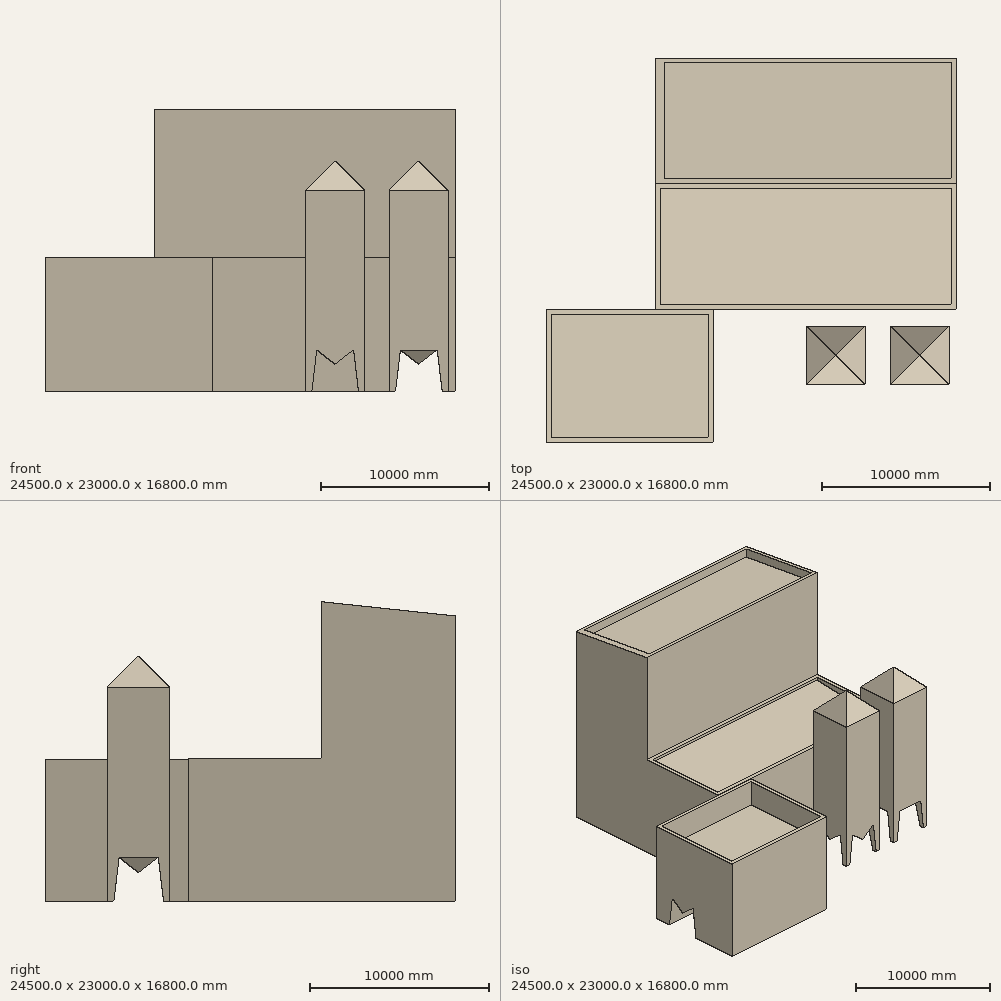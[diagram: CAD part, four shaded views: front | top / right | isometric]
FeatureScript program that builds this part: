
annotation { "Feature Type Name" : "Feature", "Feature Type Description" : "" }
export const myFeature = defineFeature(function(context is Context, id is Id, definition is map)
    precondition{}
    {
        {
            var Q0;
            Q0=qCreatedBy(makeId("Top.planeOp"),FACE);
            var sketch = newSketch(context, id + "F0", { "sketchPlane" : qUnion([Q0])});
            skLineSegment(sketch, "E0.bottom", {"start": v(0, 0) * mm, "end": v(18000, 0) * mm});
            skLineSegment(sketch, "E0.top", {"start": v(0, 7500) * mm, "end": v(18000, 7500) * mm});
            skLineSegment(sketch, "E0.left", {"start": v(0, 0) * mm, "end": v(0, 7500) * mm});
            skLineSegment(sketch, "E0.right", {"start": v(18000, 0) * mm, "end": v(18000, 7500) * mm});
            skLineSegment(sketch, "E1.top", {"start": v(0, 15000) * mm, "end": v(18000, 15000) * mm});
            skLineSegment(sketch, "E1.left", {"start": v(0, 7500) * mm, "end": v(0, 15000) * mm});
            skLineSegment(sketch, "E1.right", {"start": v(18000, 7500) * mm, "end": v(18000, 15000) * mm});
            skLineSegment(sketch, "E2.bottom", {"start": v(3500, 0) * mm, "end": v(-6500, 0) * mm});
            skLineSegment(sketch, "E2.top", {"start": v(3500, -8000) * mm, "end": v(-6500, -8000) * mm});
            skLineSegment(sketch, "E2.left", {"start": v(3500, 0) * mm, "end": v(3500, -8000) * mm});
            skLineSegment(sketch, "E2.right", {"start": v(-6500, 0) * mm, "end": v(-6500, -8000) * mm});
            skSolve(sketch);
        }
        {
            var Q0;
            Q0=makeQuery(id+"F0.imprint","IMPRINT",FACE,{"disambiguationData":[TD([[makeQuery(id+"F0.imprint","IMPRINT",EDGE,{"derivedFrom":sQuery(id+"F0.wireOp",EDGE,"E2.top")}),-1.0]])]});
            extrude(context, id + "F1", {"entities" : qUnion([Q0]), "depth" : 8000 * mm});
        }
        {
            var Q0;
            {var subQ1=sQuery(id+"F0.wireOp",EDGE,"E0.bottom");Q0=makeQuery(id+"F0.imprint","IMPRINT",FACE,{"disambiguationData":[TD([[makeQuery(id+"F0.imprint","IMPRINT",EDGE,{"derivedFrom":subQ1}),1.0]])]});}
            extrude(context, id + "F2", {"entities" : qUnion([Q0]), "operationType" : NewBodyOperationType.ADD, "depth" : 7000 * mm});
        }
        {
            var Q0;
            Q0=makeQuery(id+"F2.opExtrude","SWEPT_FACE",FACE,{"disambiguationData":[OSD([sQuery(id+"F0.wireOp",EDGE,"E0.left")])]});
            var sketch = newSketch(context, id + "F3", { "sketchPlane" : qUnion([Q0])});
            skLineSegment(sketch, "E3", {"start": v(-7500, 7000) * mm, "end": v(-7500, 7800) * mm});
            skLineSegment(sketch, "E4", {"start": v(-7500, 7800) * mm, "end": v(0, 7000) * mm});
            skLineSegment(sketch, "E5", {"start": v(0, 7000) * mm, "end": v(-7500, 7000) * mm});
            skSolve(sketch);
        }
        {
            var Q0;
            Q0 = qSketchRegion(id + "F3", true);
            var Q1;
            Q1=makeQuery(id+"F2.opExtrude","CAP_VERTEX",VERTEX,{"disambiguationData":[OSD([sQuery(id+"F0.wireOp",EDGE,"E0.right"),sQuery(id+"F0.wireOp",EDGE,"E0.top"),sQuery(id+"F0.wireOp",EDGE,"E1.right")])],"isStart":false});
            extrude(context, id + "F4", {"entities" : qUnion([Q0]), "operationType" : NewBodyOperationType.ADD, "endBound" : BoundingType.UP_TO_VERTEX, "oppositeDirection" : true, "endBoundEntityVertex" : qUnion([Q1]), "depth" : 25 * mm});
        }
        {
            var Q0;
            Q0=makeQuery(id+"F0.imprint","IMPRINT",FACE,{"disambiguationData":[TD([[makeQuery(id+"F0.imprint","IMPRINT",EDGE,{"derivedFrom":sQuery(id+"F0.wireOp",EDGE,"E0.top")}),1.0]])]});
            extrude(context, id + "F5", {"entities" : qUnion([Q0]), "operationType" : NewBodyOperationType.ADD, "depth" : 16000 * mm});
        }
        {
            var Q0;
            Q0=makeQuery(id+"F5.boolean.opBoolean","MERGE",FACE,{"derivedFrom":[makeQuery(id+"F4.boolean.opBoolean","MERGE",FACE,{"derivedFrom":[makeQuery(id+"F2.opExtrude","SWEPT_FACE",FACE,{"disambiguationData":[OSD([sQuery(id+"F0.wireOp",EDGE,"E0.left")])]}),makeQuery(id+"F4.opExtrude","CAP_FACE",FACE,{"disambiguationData":[OSD([sQuery(id+"F3.wireOp",EDGE,"E3"),sQuery(id+"F3.wireOp",EDGE,"E4"),sQuery(id+"F3.wireOp",EDGE,"E5")])],"isStart":true})]}),makeQuery(id+"F5.opExtrude","SWEPT_FACE",FACE,{"disambiguationData":[OSD([sQuery(id+"F0.wireOp",EDGE,"E1.left")])]})]});
            var sketch = newSketch(context, id + "F6", { "sketchPlane" : qUnion([Q0])});
            skLineSegment(sketch, "E6", {"start": v(-7500, 16000) * mm, "end": v(-7500, 16800) * mm});
            skLineSegment(sketch, "E7", {"start": v(-7500, 16800) * mm, "end": v(-15000, 16000) * mm});
            skLineSegment(sketch, "E8", {"start": v(-7500, 16000) * mm, "end": v(-15000, 16000) * mm});
            skSolve(sketch);
        }
        {
            var Q0;
            Q0 = qSketchRegion(id + "F6", true);
            var Q1;
            Q1=makeQuery(id+"F5.opExtrude","CAP_VERTEX",VERTEX,{"disambiguationData":[OSD([sQuery(id+"F0.wireOp",EDGE,"E0.right"),sQuery(id+"F0.wireOp",EDGE,"E0.top"),sQuery(id+"F0.wireOp",EDGE,"E1.right")])],"isStart":false});
            extrude(context, id + "F7", {"entities" : qUnion([Q0]), "operationType" : NewBodyOperationType.ADD, "endBound" : BoundingType.UP_TO_VERTEX, "oppositeDirection" : true, "endBoundEntityVertex" : qUnion([Q1]), "depth" : 25 * mm});
        }
        {
            var Q0;
            Q0=qCreatedBy(makeId("Top.planeOp"),FACE);
            cPlane(context, id + "F8", {"entities" : qUnion([Q0]), "cplaneType" : CPlaneType.OFFSET, "offset" : 8000 * mm, "width" : 150 * mm, "height" : 150 * mm});
        }
        {
            var Q0;
            Q0=makeQuery(id+"F1.opExtrude","CAP_FACE",FACE,{"disambiguationData":[OSD([sQuery(id+"F0.wireOp",EDGE,"E2.bottom"),sQuery(id+"F0.wireOp",EDGE,"E2.top"),sQuery(id+"F0.wireOp",EDGE,"E2.left"),sQuery(id+"F0.wireOp",EDGE,"E2.right")])],"isStart":false});
            extrude(context, id + "F9", {"entities" : qUnion([Q0]), "operationType" : NewBodyOperationType.REMOVE, "oppositeDirection" : true, "depth" : 25 * mm});
        }
        {
            var Q0;
            Q0=makeQuery(id+"F9.boolean.opBoolean","COPY",FACE,{"derivedFrom":makeQuery(id+"F9.opExtrude","CAP_FACE",FACE,{"disambiguationData":[OSD([sQuery(id+"F0.wireOp",EDGE,"E2.bottom"),sQuery(id+"F0.wireOp",EDGE,"E2.top"),sQuery(id+"F0.wireOp",EDGE,"E2.left"),sQuery(id+"F0.wireOp",EDGE,"E2.right")])],"isStart":false})});
            var sketch = newSketch(context, id + "F10", { "sketchPlane" : qUnion([Q0])});
            skLineSegment(sketch, "E9.0", {"start": v(3200, -7700) * mm, "end": v(3200, -300) * mm});
            skLineSegment(sketch, "E9.1", {"start": v(3500, -300) * mm, "end": v(3082.9, -300) * mm});
            skLineSegment(sketch, "E9.2", {"start": v(3082.9, -300) * mm, "end": v(-6200, -300) * mm});
            skLineSegment(sketch, "E9.3", {"start": v(3500, -300) * mm, "end": v(3200, -300) * mm});
            skLineSegment(sketch, "E9.4", {"start": v(-6200, -300) * mm, "end": v(-6200, -7700) * mm});
            skLineSegment(sketch, "E9.5", {"start": v(-6200, -7700) * mm, "end": v(3200, -7700) * mm});
            skLineSegment(sketch, "E10.0", {"start": v(3505, -8005) * mm, "end": v(3505, 5) * mm});
            skLineSegment(sketch, "E10.1", {"start": v(3500, 5) * mm, "end": v(3387.9, 5) * mm});
            skLineSegment(sketch, "E10.2", {"start": v(3387.9, 5) * mm, "end": v(-6505, 5) * mm});
            skLineSegment(sketch, "E10.3", {"start": v(3505, 5) * mm, "end": v(3500, 5) * mm});
            skLineSegment(sketch, "E10.4", {"start": v(-6505, 5) * mm, "end": v(-6505, -8005) * mm});
            skLineSegment(sketch, "E10.5", {"start": v(-6505, -8005) * mm, "end": v(3505, -8005) * mm});
            skSolve(sketch);
        }
        {
            var Q0;
            Q0=makeQuery(id+"F10.imprint","IMPRINT",FACE,{"disambiguationData":[TD([[makeQuery(id+"F10.imprint","IMPRINT",EDGE,{"derivedFrom":sQuery(id+"F10.wireOp",EDGE,"E9.0")}),1.0]])]});
            extrude(context, id + "F11", {"entities" : qUnion([Q0]), "operationType" : NewBodyOperationType.REMOVE, "oppositeDirection" : true, "depth" : 2000 * mm});
        }
        {
            var Q0;
            Q0=qCreatedBy(id+"F8.planeOp",FACE);
            var sketch = newSketch(context, id + "F12", { "sketchPlane" : qUnion([Q0])});
            skLineSegment(sketch, "E11.0.0", {"start": v(18000, 0) * mm, "end": v(18000, 7500) * mm});
            skLineSegment(sketch, "E11.0.1", {"start": v(18000, 7500) * mm, "end": v(0, 7500) * mm});
            skLineSegment(sketch, "E11.0.2", {"start": v(0, 7500) * mm, "end": v(0, 0) * mm});
            skLineSegment(sketch, "E11.0.4", {"start": v(0, 0) * mm, "end": v(18000, 0) * mm});
            skPoint(sketch, "E12.orphan", {"position": v(3500, 0) * mm});
            skLineSegment(sketch, "E13.0", {"start": v(300, 7200) * mm, "end": v(300, 300) * mm});
            skLineSegment(sketch, "E13.1", {"start": v(17700, 7200) * mm, "end": v(300, 7200) * mm});
            skLineSegment(sketch, "E13.2", {"start": v(17700, 300) * mm, "end": v(17700, 7200) * mm});
            skLineSegment(sketch, "E13.3", {"start": v(300, 300) * mm, "end": v(17700, 300) * mm});
            skSolve(sketch);
        }
        {
            var Q0;
            Q0 = qSketchRegion(id + "F12", true);
            var Q1;
            Q1=makeQuery(id+"F4.opExtrude","SWEPT_FACE",FACE,{"disambiguationData":[OSD([sQuery(id+"F3.wireOp",EDGE,"E4")])]});
            extrude(context, id + "F13", {"entities" : qUnion([Q0]), "operationType" : NewBodyOperationType.ADD, "endBound" : BoundingType.UP_TO_SURFACE, "oppositeDirection" : true, "endBoundEntityFace" : qUnion([Q1]), "depth" : 25 * mm});
        }
        {
            var Q0;
            Q0=qCreatedBy(makeId("Top.planeOp"),FACE);
            var sketch = newSketch(context, id + "F14", { "sketchPlane" : qUnion([Q0])});
            skLineSegment(sketch, "E14.bottom", {"start": v(17561.13, -1019.75) * mm, "end": v(14061.13, -1019.75) * mm});
            skLineSegment(sketch, "E14.top", {"start": v(17561.13, -4519.75) * mm, "end": v(14061.13, -4519.75) * mm});
            skLineSegment(sketch, "E14.left", {"start": v(17561.13, -1019.75) * mm, "end": v(17561.13, -4519.75) * mm});
            skLineSegment(sketch, "E14.right", {"start": v(14061.13, -1019.75) * mm, "end": v(14061.13, -4519.75) * mm});
            skSolve(sketch);
        }
        {
            var Q0;
            Q0 = qSketchRegion(id + "F14", true);
            extrude(context, id + "F15", {"entities" : qUnion([Q0]), "depth" : 12000 * mm});
        }
        {
            var Q0;
            Q0=makeQuery(id+"F15.opExtrude","CAP_FACE",FACE,{"disambiguationData":[OSD([sQuery(id+"F14.wireOp",EDGE,"E14.bottom"),sQuery(id+"F14.wireOp",EDGE,"E14.top"),sQuery(id+"F14.wireOp",EDGE,"E14.left"),sQuery(id+"F14.wireOp",EDGE,"E14.right")])],"isStart":false});
            extrude(context, id + "F16", {"entities" : qUnion([Q0]), "operationType" : NewBodyOperationType.ADD, "depth" : 2000 * mm, "hasDraft" : true, "draftAngle" : 45 * degree, "draftPullDirection" : true});
        }
        {
            var Q0;
            Q0=makeQuery(id+"F15.opExtrude","SWEPT_FACE",FACE,{"disambiguationData":[OSD([sQuery(id+"F14.wireOp",EDGE,"E14.left")])]});
            var sketch = newSketch(context, id + "F17", { "sketchPlane" : qUnion([Q0])});
            skLineSegment(sketch, "E15", {"start": v(-4159.8, 0) * mm, "end": v(-3869.57, 2452.53) * mm});
            skLineSegment(sketch, "E16", {"start": v(-2769.75, 12000) * mm, "end": v(-2769.75, 0) * mm, "construction": true});
            skLineSegment(sketch, "E17", {"start": v(-3869.57, 2452.53) * mm, "end": v(-2769.75, 1592.63) * mm});
            skLineSegment(sketch, "E18", {"start": v(-4159.8, 0) * mm, "end": v(-2769.75, 0) * mm});
            skLineSegment(sketch, "E19.MirrorCS", {"start": v(-1379.7, 0) * mm, "end": v(-2769.75, 0) * mm});
            skLineSegment(sketch, "E20.MirrorCS", {"start": v(-1669.93, 2452.53) * mm, "end": v(-2769.75, 1592.63) * mm});
            skLineSegment(sketch, "E21.MirrorCS", {"start": v(-1379.7, 0) * mm, "end": v(-1669.93, 2452.53) * mm});
            skSolve(sketch);
        }
        {
            var Q0;
            Q0 = qSketchRegion(id + "F17", true);
            extrude(context, id + "F18", {"entities" : qUnion([Q0]), "operationType" : NewBodyOperationType.REMOVE, "endBound" : BoundingType.THROUGH_ALL, "oppositeDirection" : true, "depth" : 25 * mm});
        }
        {
            var Q0;
            Q0=makeQuery(id+"F15.opExtrude","SWEPT_FACE",FACE,{"disambiguationData":[OSD([sQuery(id+"F14.wireOp",EDGE,"E14.top")])]});
            var sketch = newSketch(context, id + "F19", { "sketchPlane" : qUnion([Q0])});
            skLineSegment(sketch, "E22", {"start": v(14421.1, 0) * mm, "end": v(14711.3, 2452.53) * mm});
            skLineSegment(sketch, "E23", {"start": v(15811.13, 12000) * mm, "end": v(15811.13, 0) * mm, "construction": true});
            skLineSegment(sketch, "E24", {"start": v(14711.3, 2452.53) * mm, "end": v(15811.13, 1592.63) * mm});
            skLineSegment(sketch, "E25", {"start": v(14421.1, 0) * mm, "end": v(15811.13, 0) * mm});
            skLineSegment(sketch, "E26.MirrorCS", {"start": v(17201.18, 0) * mm, "end": v(15811.13, 0) * mm});
            skLineSegment(sketch, "E27.MirrorCS", {"start": v(16910.96, 2452.53) * mm, "end": v(15811.13, 1592.63) * mm});
            skLineSegment(sketch, "E28.MirrorCS", {"start": v(17201.18, 0) * mm, "end": v(16910.96, 2452.53) * mm});
            skSolve(sketch);
        }
        {
            var Q0;
            Q0 = qSketchRegion(id + "F19", true);
            extrude(context, id + "F20", {"entities" : qUnion([Q0]), "operationType" : NewBodyOperationType.REMOVE, "endBound" : BoundingType.THROUGH_ALL, "oppositeDirection" : true, "depth" : 25 * mm});
        }
        {
            var Q0;
            Q0=makeQuery(id+"F15.opExtrude","SWEPT_BODY",BODY,{"disambiguationData":[OSD([sQuery(id+"F14.wireOp",EDGE,"E14.bottom"),sQuery(id+"F14.wireOp",EDGE,"E14.top"),sQuery(id+"F14.wireOp",EDGE,"E14.left"),sQuery(id+"F14.wireOp",EDGE,"E14.right")])]});
            transform(context, id + "F21", {"entities" : qUnion([Q0]), "transformType" : TransformType.TRANSLATION_3D, "dx" : -5000 * mm, "dy" : 0 * mm, "dz" : 0 * mm, "makeCopy" : true});
        }
        {
            var Q0;
            {var subQ0=sQuery(id+"F14.wireOp",EDGE,"E14.top");var subQ1=makeQuery(id+"F15.opExtrude","SWEPT_FACE",FACE,{"disambiguationData":[OSD([subQ0])]});var subQ2=sQuery(id+"F14.wireOp",EDGE,"E14.right");var subQ3=makeQuery(id+"F15.opExtrude","SWEPT_FACE",FACE,{"disambiguationData":[OSD([subQ2])]});var subQ5=sQuery(id+"F14.wireOp",EDGE,"E14.left");Q0=makeQuery(id+"F20.boolean.opBoolean","SPLIT",FACE,{"disambiguationData":[TD([subQ3])],"derivedFrom":makeQuery(id+"F18.boolean.opBoolean","SPLIT",FACE,{"disambiguationData":[TD([subQ1])],"derivedFrom":makeQuery(id+"F15.opExtrude","CAP_FACE",FACE,{"disambiguationData":[OSD([sQuery(id+"F14.wireOp",EDGE,"E14.bottom"),subQ0,subQ5,subQ2])],"isStart":true})})});}
            var sketch = newSketch(context, id + "F22", { "sketchPlane" : qUnion([Q0])});
            skLineSegment(sketch, "E29.0", {"start": v(16910.96, 3869.57) * mm, "end": v(16910.96, 4519.75) * mm});
            skLineSegment(sketch, "E29.1", {"start": v(14711.3, 3869.57) * mm, "end": v(16910.96, 3869.57) * mm});
            skLineSegment(sketch, "E29.2", {"start": v(14711.3, 3869.57) * mm, "end": v(14711.3, 4519.75) * mm});
            skLineSegment(sketch, "E29.3", {"start": v(14711.3, 4519.75) * mm, "end": v(15811.13, 4519.75) * mm});
            skLineSegment(sketch, "E29.4", {"start": v(16910.96, 4519.75) * mm, "end": v(15811.13, 4519.75) * mm});
            skLineSegment(sketch, "E29.5", {"start": v(14711.3, 1669.93) * mm, "end": v(14711.3, 3869.57) * mm});
            skLineSegment(sketch, "E29.6", {"start": v(14711.3, 1669.93) * mm, "end": v(16910.96, 1669.93) * mm});
            skLineSegment(sketch, "E29.7", {"start": v(16910.96, 1669.93) * mm, "end": v(16910.96, 3869.57) * mm});
            skLineSegment(sketch, "E29.8", {"start": v(16910.96, 3869.57) * mm, "end": v(17561.13, 3869.57) * mm});
            skLineSegment(sketch, "E29.9", {"start": v(17561.13, 3869.57) * mm, "end": v(17561.13, 2769.75) * mm});
            skLineSegment(sketch, "E29.10", {"start": v(17561.13, 1669.93) * mm, "end": v(17561.13, 2769.75) * mm});
            skLineSegment(sketch, "E29.11", {"start": v(16910.96, 1669.93) * mm, "end": v(17561.13, 1669.93) * mm});
            skLineSegment(sketch, "E29.12", {"start": v(16910.96, 1019.75) * mm, "end": v(16910.96, 1669.93) * mm});
            skLineSegment(sketch, "E29.13", {"start": v(14711.3, 1019.75) * mm, "end": v(14711.3, 1669.93) * mm});
            skLineSegment(sketch, "E29.14", {"start": v(14711.3, 1019.75) * mm, "end": v(15811.13, 1019.75) * mm});
            skLineSegment(sketch, "E29.15", {"start": v(16910.96, 1019.75) * mm, "end": v(15811.13, 1019.75) * mm});
            skLineSegment(sketch, "E29.16", {"start": v(14061.13, 1669.93) * mm, "end": v(14711.3, 1669.93) * mm});
            skLineSegment(sketch, "E29.17", {"start": v(14061.13, 1669.93) * mm, "end": v(14061.13, 2769.75) * mm});
            skLineSegment(sketch, "E29.18", {"start": v(14061.13, 3869.57) * mm, "end": v(14061.13, 2769.75) * mm});
            skLineSegment(sketch, "E29.19", {"start": v(14061.13, 3869.57) * mm, "end": v(14711.3, 3869.57) * mm});
            skPoint(sketch, "E29.20", {"position": v(17236.04, 3869.57) * mm});
            skPoint(sketch, "E29.21", {"position": v(14386.22, 3869.57) * mm});
            skSolve(sketch);
        }
        {
            var Q0;
            Q0=makeQuery(id+"F22.imprint","IMPRINT",FACE,{"disambiguationData":[TD([[makeQuery(id+"F22.imprint","IMPRINT",EDGE,{"derivedFrom":sQuery(id+"F22.wireOp",EDGE,"E29.0")}),1.0]])]});
            var Q1;
            Q1=makeQuery(id+"F22.imprint","IMPRINT",FACE,{"disambiguationData":[TD([[makeQuery(id+"F22.imprint","IMPRINT",EDGE,{"derivedFrom":sQuery(id+"F22.wireOp",EDGE,"E29.7")}),-1.0]])]});
            var Q2;
            Q2=makeQuery(id+"F22.imprint","IMPRINT",FACE,{"disambiguationData":[TD([[makeQuery(id+"F22.imprint","IMPRINT",EDGE,{"derivedFrom":sQuery(id+"F22.wireOp",EDGE,"E29.6")}),-1.0]])]});
            var Q3;
            Q3=makeQuery(id+"F22.imprint","IMPRINT",FACE,{"disambiguationData":[TD([[makeQuery(id+"F22.imprint","IMPRINT",EDGE,{"derivedFrom":sQuery(id+"F22.wireOp",EDGE,"E29.5")}),1.0]])]});
            var Q4;
            Q4=makeQuery(id+"F20.boolean.opBoolean","COPY",VERTEX,{"derivedFrom":makeQuery(id+"F20.opExtrude","CAP_VERTEX",VERTEX,{"disambiguationData":[OSD([sQuery(id+"F19.wireOp",EDGE,"E22"),sQuery(id+"F19.wireOp",EDGE,"E24")])],"isStart":true})});
            extrude(context, id + "F23", {"entities" : qUnion([Q0, Q1, Q2, Q3]), "operationType" : NewBodyOperationType.REMOVE, "endBound" : BoundingType.UP_TO_VERTEX, "oppositeDirection" : true, "endBoundEntityVertex" : qUnion([Q4]), "depth" : 1900 * mm});
        }
        {
            var Q0;
            Q0=makeQuery(id+"F13.boolean.opBoolean","MERGE",FACE,{"derivedFrom":[makeQuery(id+"F7.boolean.opBoolean","MERGE",FACE,{"derivedFrom":[makeQuery(id+"F5.boolean.opBoolean","MERGE",FACE,{"derivedFrom":[makeQuery(id+"F4.boolean.opBoolean","MERGE",FACE,{"derivedFrom":[makeQuery(id+"F2.opExtrude","SWEPT_FACE",FACE,{"disambiguationData":[OSD([sQuery(id+"F0.wireOp",EDGE,"E0.right")])]}),makeQuery(id+"F4.opExtrude","CAP_FACE",FACE,{"disambiguationData":[OSD([dummyQuery(id+"F4.vertexPlane.planeOp",FACE)])],"isStart":false})]}),makeQuery(id+"F5.opExtrude","SWEPT_FACE",FACE,{"disambiguationData":[OSD([sQuery(id+"F0.wireOp",EDGE,"E1.right")])]})]}),makeQuery(id+"F7.opExtrude","CAP_FACE",FACE,{"disambiguationData":[OSD([dummyQuery(id+"F7.vertexPlane.planeOp",FACE)])],"isStart":false})]}),makeQuery(id+"F13.opExtrude","SWEPT_FACE",FACE,{"disambiguationData":[OSD([sQuery(id+"F12.wireOp",EDGE,"E11.0.0")])]})]});
            cPlane(context, id + "F24", {"entities" : qUnion([Q0]), "cplaneType" : CPlaneType.OFFSET, "offset" : 300 * mm, "oppositeDirection" : true, "width" : 150 * mm, "height" : 150 * mm});
        }
        {
            var Q0;
            Q0=qCreatedBy(id+"F24.planeOp",FACE);
            var sketch = newSketch(context, id + "F25", { "sketchPlane" : qUnion([Q0])});
            skLineSegment(sketch, "E30.0", {"start": v(7800, 16773.03) * mm, "end": v(7800, 16069.06) * mm});
            skLineSegment(sketch, "E31.0", {"start": v(15005, 16004.5) * mm, "end": v(7495, 16805.56) * mm});
            skLineSegment(sketch, "E31.1", {"start": v(7495, 8005) * mm, "end": v(-5, 8005) * mm});
            skLineSegment(sketch, "E31.2", {"start": v(-5, 8005) * mm, "end": v(-5, -5) * mm});
            skLineSegment(sketch, "E31.3", {"start": v(7495, 16805.56) * mm, "end": v(7495, 8005) * mm});
            skLineSegment(sketch, "E31.4", {"start": v(-5, -5) * mm, "end": v(15005, -5) * mm});
            skLineSegment(sketch, "E31.5", {"start": v(15005, -5) * mm, "end": v(15005, 16004.5) * mm});
            skLineSegment(sketch, "E32.0", {"start": v(14705, 15332.52) * mm, "end": v(14705, 16036.5) * mm});
            skLineSegment(sketch, "E33.0", {"start": v(14705, 15332.52) * mm, "end": v(7800, 16069.06) * mm});
            skSolve(sketch);
        }
        {
            var Q0;
            {var subQ0=sQuery(id+"F25.wireOp",EDGE,"E30.0");Q0=makeQuery(id+"F25.imprint","IMPRINT",FACE,{"disambiguationData":[TD([[makeQuery(id+"F25.imprint","IMPRINT",EDGE,{"derivedFrom":subQ0}),1.0]])]});}
            extrude(context, id + "F26", {"entities" : qUnion([Q0]), "operationType" : NewBodyOperationType.REMOVE, "oppositeDirection" : true, "depth" : 17120 * mm, "offsetDistance" : 25 * mm});
        }
    });
